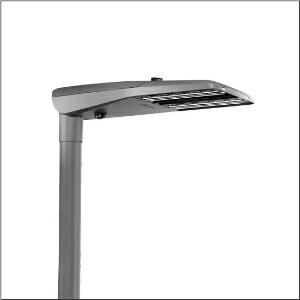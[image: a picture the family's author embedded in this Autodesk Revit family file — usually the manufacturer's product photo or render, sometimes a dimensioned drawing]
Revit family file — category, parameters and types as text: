
# Revit family: streetlight_sl_11_iq_midi___pc-l_5xc3e51y08me_36d5
name_source: partatom
category: Lighting Fixtures
units: mm (PartAtom-declared; Revit-internal decimal feet)

## family parameters
Cut with Voids When Loaded = No
Host = Face
Light Source = No
Part Type = Normal
Room Calculation Point = No
Round Connector Dimension = Use Diameter
Shared = No

## types (1)
- --- (1 x LED, 15540 lm, 122.7 W, 3000K)
    Apparent Load = 123 VA
    CIE Flux Codes = 37 73 96 100 100
    Color Rendering = 70
    Color Temperature = 3000K
    Default Elevation = 1800 mm
    Description = Streetlight SL 11 iQ midi, mast luminaire, primary light control with 3 zone facetted reflector, of plastic, silver coated, highly specular, primary optical cover: cover, of PMMA, transparent, light distribution: PC-L, light emission: direct distribution, primary light characteristic: asymmetric, left, installation type: post-top, side-entry, LED, High Power LED, rated luminous flux: 15.540lm, luminous efficacy: 127lm/W, light colour: 730, colour temperature: 3000K, control: presetting dimming logarithmic, Street-Remote, Auto-Match, Temp-Guard, Lumen-Switch, Night-Set, Smart-Wire, Light-Fading, Desk-Remote (wireless, voltage-free reading and setting of iQ features in the workshop via application-optimized NFC function/RFID function), optimised constant luminous flux control (CLO 2.0), with cable H07RN-F 5x 1.5mm², mains connection: 230..240V, AC, 50/60Hz, connection cable pre-assembled, cable length: 12,5m, start of lifetime: 123W, end of service life: 130W, reduction: 56W, luminaire housing, of diecast aluminium, powder-coated, Siteco® metallic grey (DB 702S), please order mast flange separately, inclination adjustable without tools: 0°, 5°, 10°, 15° (post-top) | 0°, -5°, -10°, -15° (side-entry), sealing non-destructively replaceable, multi-level sealing system, length: 780mm, width: 376mm, height: 118mm, mast flange for spigot size: 42mm (side-entry): 5XC10008XM4, 60/48mm (side-entry/post-top): 5XC10108XM2, 76/60mm (side-entry/post-top): 5XC10108XM1, equipment: Power, Smart Interface below and above, protection rating (complete): IP66, insulation class (complete): insulation class II (safety insulation), certification: CE, ENEC, VDE, UKCA, impact resistance: IK09, permissible operating ambient temperature for outdoor applications: -25..+50°C, standard-compliant lighting for roads and squares, Environmental Product Declaration (EPD) tested and certified by an independent institute, packaging unit: 1 piece

Light Distribution: PC-L
    Height = 118 mm
    Lamp = 1 x LED
    Lamp Light Flux = 15540 lm
    Lamp Power = 122.7 W
    Lamp count = 1
    Length = 780 mm
    Luminous efficacy = 127 lm/W
    Manufacturer = Siteco
    ModVariant = No
    Model = 5XC3E51Y08ME
    Number of Poles = 1
    OnlyDefault = Yes
    Power Factor = 1
    Product Name = Streetlight SL 11 iQ midi | PC-L
    Product group = mast luminaire | pylon top
    ProductGroupID = 6100
    Protection Class = Protection class II
    Protection Degree = IP 66
    RLX_Detail_Level = 1
    RLX_Emergency_Light_Flux = 0 lm
    RLX_Emergency_Type = 0
    RLX_Emergency_Type_DB = No
    RlxData = <blob elided: 73529 chars, md5=1568a376>
    Socket = socket
    Standby Power = 0 W
    System Light Flux = 15540 lm
    System Power = 123 W
    Type Comments = factory setting: luminous flux: 100 % | dim-lin: 254 | 552 mA
    Type Image = l_1004429.jpg
    URL = http://relux.com
    VarID = @adj_082339
    Voltage = 0 V
    Weight = 0.00 kg
    Width = 376 mm

## geometry (parser evidence)
native form markers: Blend x4, Sweep x12
no freeform markers — native parametric forms only
